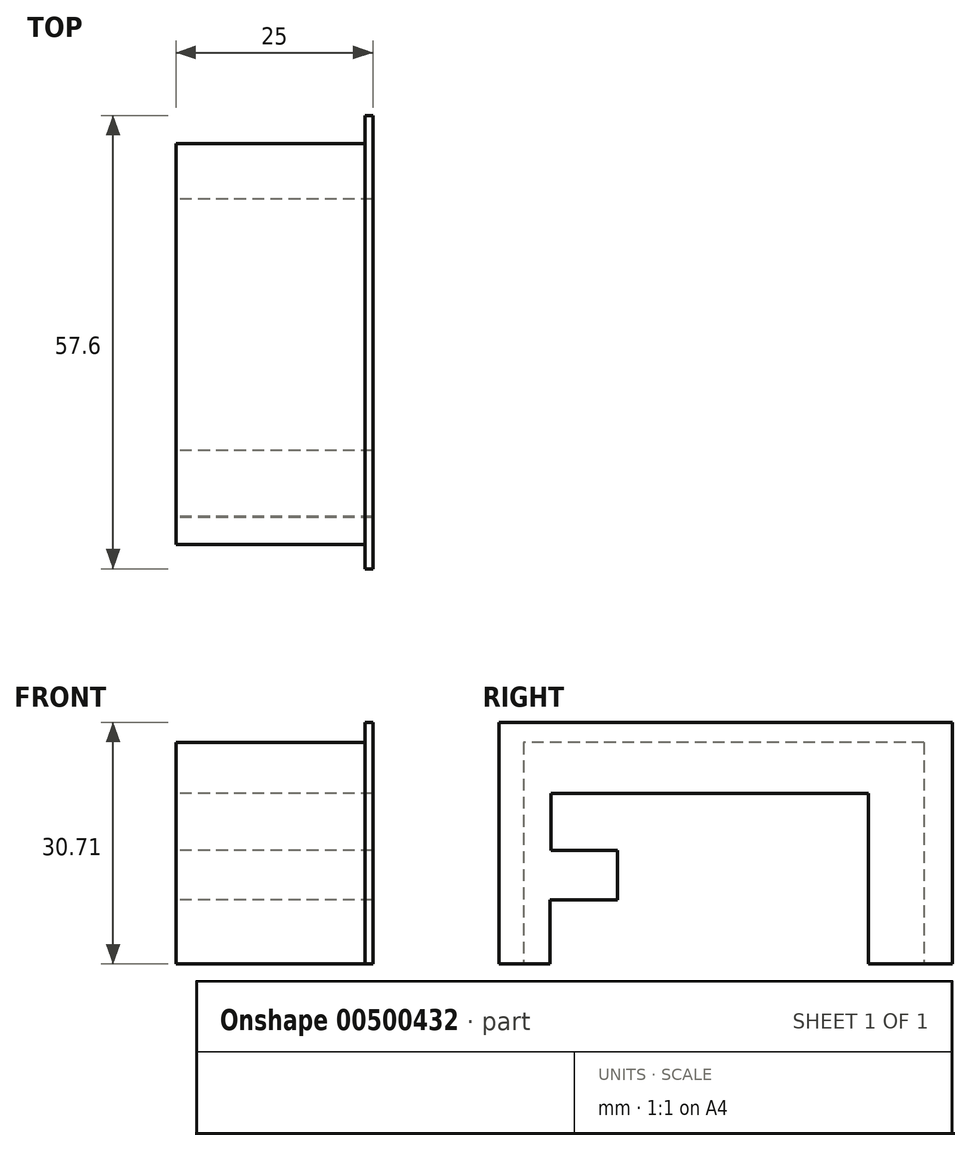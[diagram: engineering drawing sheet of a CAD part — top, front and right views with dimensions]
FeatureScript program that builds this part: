
annotation { "Feature Type Name" : "Feature", "Feature Type Description" : "" }
export const myFeature = defineFeature(function(context is Context, id is Id, definition is map)
    precondition{}
    {
        {
            var Q0;
            Q0=qCreatedBy(makeId("Right.planeOp"),FACE);
            var sketch = newSketch(context, id + "F0", { "sketchPlane" : qUnion([Q0])});
            skLineSegment(sketch, "E0.bottom", {"start": v(0, 0) * mm, "end": v(6.5, 0) * mm});
            skLineSegment(sketch, "E0.top", {"start": v(0, 30.7) * mm, "end": v(57.6, 30.7) * mm});
            skLineSegment(sketch, "E0.left", {"start": v(0, 0) * mm, "end": v(0, 30.7) * mm});
            skLineSegment(sketch, "E0.right", {"start": v(57.6, 0) * mm, "end": v(57.6, 30.7) * mm});
            skLineSegment(sketch, "E1", {"start": v(6.5, 0) * mm, "end": v(6.5, 8.17) * mm});
            skLineSegment(sketch, "E2", {"start": v(6.5, 8.17) * mm, "end": v(15.05, 8.17) * mm});
            skLineSegment(sketch, "E3", {"start": v(15.05, 8.17) * mm, "end": v(15.05, 14.44) * mm});
            skLineSegment(sketch, "E4", {"start": v(15.05, 14.44) * mm, "end": v(6.64, 14.44) * mm});
            skLineSegment(sketch, "E5", {"start": v(6.64, 14.44) * mm, "end": v(6.64, 21.7) * mm});
            skLineSegment(sketch, "E6", {"start": v(6.64, 21.7) * mm, "end": v(46.97, 21.7) * mm});
            skLineSegment(sketch, "E7", {"start": v(46.97, 21.7) * mm, "end": v(46.97, 0) * mm});
            skLineSegment(sketch, "E8.trimOffspring", {"start": v(46.97, 0) * mm, "end": v(57.6, 0) * mm});
            skSolve(sketch);
        }
        {
            var Q0;
            Q0=makeQuery(id+"F0.imprint","IMPRINT",FACE,{"disambiguationData":[TD([[makeQuery(id+"F0.imprint","IMPRINT",EDGE,{"derivedFrom":sQuery(id+"F0.wireOp",EDGE,"E0.bottom")}),1.0]])]});
            extrude(context, id + "F1", {"entities" : qUnion([Q0]), "depth" : 25 * mm});
        }
        {
            var Q0;
            Q0=makeQuery(id+"F1.opExtrude","CAP_FACE",FACE,{"disambiguationData":[OSD([sQuery(id+"F0.wireOp",EDGE,"E0.bottom"),sQuery(id+"F0.wireOp",EDGE,"E0.top"),sQuery(id+"F0.wireOp",EDGE,"E0.left"),sQuery(id+"F0.wireOp",EDGE,"E0.right"),sQuery(id+"F0.wireOp",EDGE,"E1"),sQuery(id+"F0.wireOp",EDGE,"E2"),sQuery(id+"F0.wireOp",EDGE,"E3"),sQuery(id+"F0.wireOp",EDGE,"E4"),sQuery(id+"F0.wireOp",EDGE,"E5"),sQuery(id+"F0.wireOp",EDGE,"E6"),sQuery(id+"F0.wireOp",EDGE,"E7"),sQuery(id+"F0.wireOp",EDGE,"E8.trimOffspring")])],"isStart":true});
            var sketch = newSketch(context, id + "F2", { "sketchPlane" : qUnion([Q0])});
            skLineSegment(sketch, "E9", {"start": v(-54, 28.14) * mm, "end": v(-3.11, 28.14) * mm});
            skLineSegment(sketch, "E10", {"start": v(-3.11, 28.14) * mm, "end": v(-3.11, 0) * mm});
            skLineSegment(sketch, "E11", {"start": v(-54, -2.16) * mm, "end": v(-65.97, -2.16) * mm});
            skLineSegment(sketch, "E12", {"start": v(-65.97, -2.16) * mm, "end": v(-65.97, 33.47) * mm});
            skLineSegment(sketch, "E13", {"start": v(-65.97, 33.47) * mm, "end": v(2.57, 33.47) * mm});
            skLineSegment(sketch, "E14", {"start": v(2.57, 33.47) * mm, "end": v(2.57, 0) * mm});
            skLineSegment(sketch, "E15", {"start": v(2.57, 0) * mm, "end": v(-3.11, 0) * mm});
            skLineSegment(sketch, "E16", {"start": v(-54, 28.14) * mm, "end": v(-54, -2.16) * mm});
            skSolve(sketch);
        }
        {
            var Q0;
            Q0 = qSketchRegion(id + "F2", true);
            extrude(context, id + "F3", {"entities" : qUnion([Q0]), "operationType" : NewBodyOperationType.REMOVE, "oppositeDirection" : true, "depth" : 24 * mm});
        }
    });
